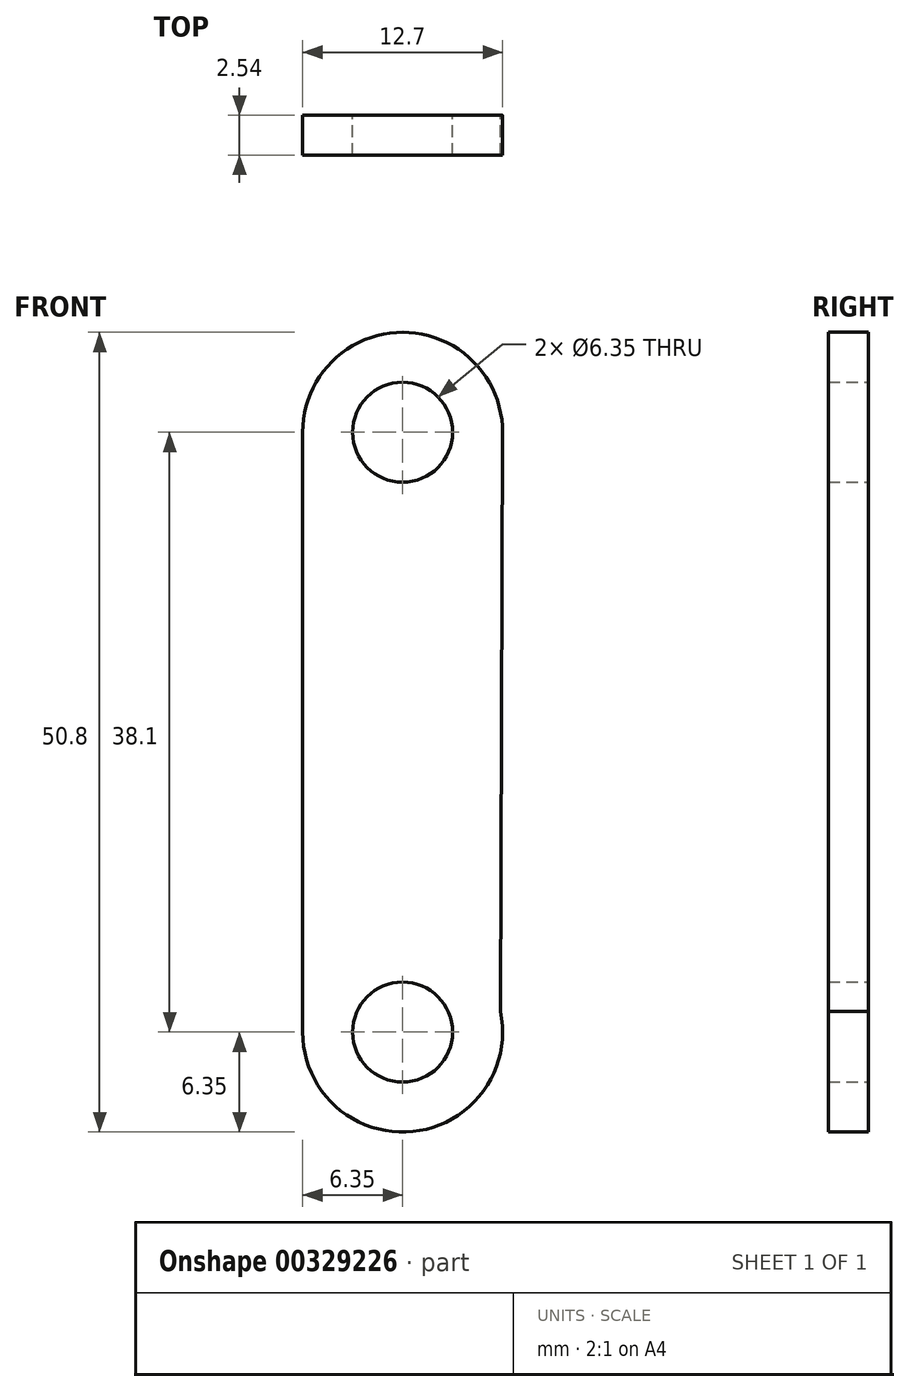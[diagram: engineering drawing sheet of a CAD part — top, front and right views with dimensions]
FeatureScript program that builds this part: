
annotation { "Feature Type Name" : "Feature", "Feature Type Description" : "" }
export const myFeature = defineFeature(function(context is Context, id is Id, definition is map)
    precondition{}
    {
        {
            var Q0;
            Q0=qCreatedBy(makeId("Front.planeOp"),FACE);
            var sketch = newSketch(context, id + "F0", { "sketchPlane" : qUnion([Q0])});
            skCircle(sketch, "E0", {"center": v(0, 0) * mm, "radius": 3.18 * mm});
            skCircle(sketch, "E1", {"center": v(0, 38.1) * mm, "radius": 6.35 * mm});
            skCircle(sketch, "E2", {"center": v(0, 38.1) * mm, "radius": 3.18 * mm});
            skCircle(sketch, "E3", {"center": v(0, 0) * mm, "radius": 6.35 * mm});
            skLineSegment(sketch, "E4", {"start": v(-6.35, 38.1) * mm, "end": v(-6.35, 0) * mm});
            skLineSegment(sketch, "E5", {"start": v(6.35, 38.08) * mm, "end": v(6.22, 1.3) * mm});
            skSolve(sketch);
        }
        {
            var Q0;
            Q0=makeQuery(id+"F0.imprint","IMPRINT",FACE,{"disambiguationData":[TD([[makeQuery(id+"F0.imprint","IMPRINT",EDGE,{"derivedFrom":sQuery(id+"F0.wireOp",EDGE,"E0")}),-1.0]])]});
            var Q1;
            {var subQ0=sQuery(id+"F0.wireOp",EDGE,"E4");Q1=makeQuery(id+"F0.imprint","IMPRINT",FACE,{"disambiguationData":[TD([[makeQuery(id+"F0.imprint","IMPRINT",EDGE,{"derivedFrom":subQ0}),1.0]])]});}
            var Q2;
            Q2=makeQuery(id+"F0.imprint","IMPRINT",FACE,{"disambiguationData":[TD([[makeQuery(id+"F0.imprint","IMPRINT",EDGE,{"derivedFrom":sQuery(id+"F0.wireOp",EDGE,"E2")}),-1.0]])]});
            extrude(context, id + "F1", {"entities" : qUnion([Q0, Q1, Q2]), "depth" : 2.54 * mm});
        }
    });
